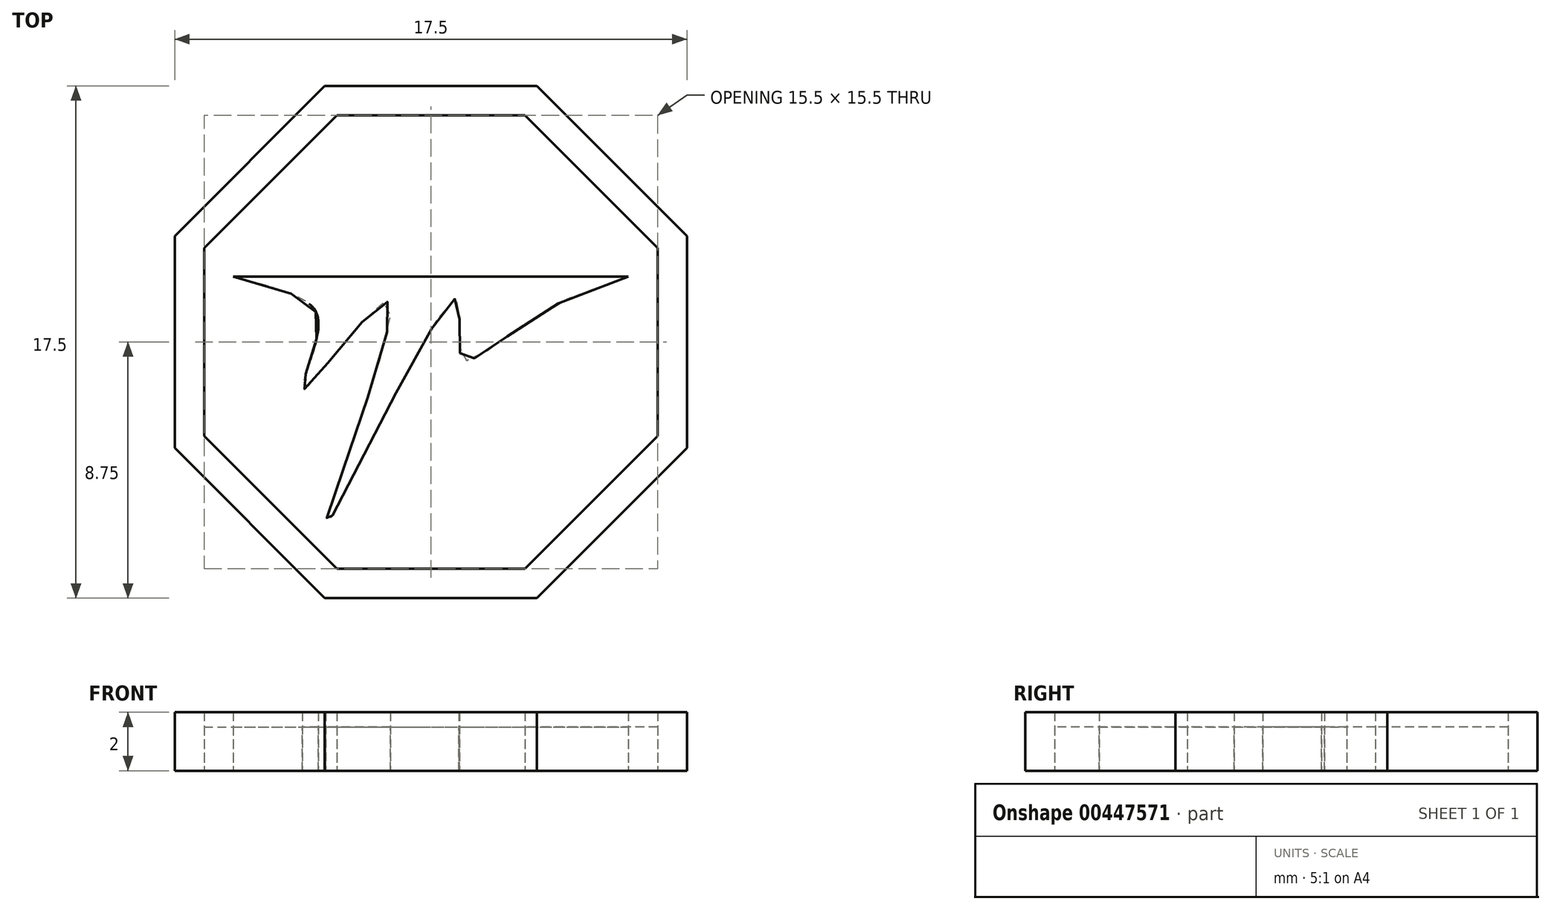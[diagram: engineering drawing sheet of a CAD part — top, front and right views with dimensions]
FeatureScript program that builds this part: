
annotation { "Feature Type Name" : "Feature", "Feature Type Description" : "" }
export const myFeature = defineFeature(function(context is Context, id is Id, definition is map)
    precondition{}
    {
        {
            var Q0;
            Q0=qCreatedBy(makeId("Top.planeOp"),FACE);
            var sketch = newSketch(context, id + "F0", { "sketchPlane" : qUnion([Q0])});
            skCircle(sketch, "E0.cCircle", {"center": v(0, 0) * mm, "radius": 8.75 * mm, "construction": true});
            skLineSegment(sketch, "E0.0", {"start": v(3.62, -8.75) * mm, "end": v(-3.62, -8.75) * mm});
            skLineSegment(sketch, "E0.1", {"start": v(-3.62, -8.75) * mm, "end": v(-8.75, -3.62) * mm});
            skLineSegment(sketch, "E0.2", {"start": v(-8.75, -3.62) * mm, "end": v(-8.75, 3.62) * mm});
            skLineSegment(sketch, "E0.3", {"start": v(-8.75, 3.62) * mm, "end": v(-3.62, 8.75) * mm});
            skLineSegment(sketch, "E0.4", {"start": v(-3.62, 8.75) * mm, "end": v(3.62, 8.75) * mm});
            skLineSegment(sketch, "E0.5", {"start": v(3.62, 8.75) * mm, "end": v(8.75, 3.62) * mm});
            skLineSegment(sketch, "E0.6", {"start": v(8.75, 3.62) * mm, "end": v(8.75, -3.62) * mm});
            skLineSegment(sketch, "E0.7", {"start": v(8.75, -3.62) * mm, "end": v(3.62, -8.75) * mm});
            skPoint(sketch, "E0.0.midPoint", {"position": v(0, -8.75) * mm});
            skCircle(sketch, "E1.cCircle", {"center": v(0, 0) * mm, "radius": 7.75 * mm, "construction": true});
            skLineSegment(sketch, "E1.0", {"start": v(7.75, -3.21) * mm, "end": v(3.21, -7.75) * mm});
            skLineSegment(sketch, "E1.1", {"start": v(3.21, -7.75) * mm, "end": v(-3.21, -7.75) * mm});
            skLineSegment(sketch, "E1.2", {"start": v(-3.21, -7.75) * mm, "end": v(-7.75, -3.21) * mm});
            skLineSegment(sketch, "E1.3", {"start": v(-7.75, -3.21) * mm, "end": v(-7.75, 3.21) * mm});
            skLineSegment(sketch, "E1.4", {"start": v(-7.75, 3.21) * mm, "end": v(-3.21, 7.75) * mm});
            skLineSegment(sketch, "E1.5", {"start": v(-3.21, 7.75) * mm, "end": v(3.21, 7.75) * mm});
            skLineSegment(sketch, "E1.6", {"start": v(3.21, 7.75) * mm, "end": v(7.75, 3.21) * mm});
            skLineSegment(sketch, "E1.7", {"start": v(7.75, 3.21) * mm, "end": v(7.75, -3.21) * mm});
            skPoint(sketch, "E1.0.midPoint", {"position": v(5.48, -5.48) * mm});
            skLineSegment(sketch, "E2", {"start": v(-6.75, 2.24) * mm, "end": v(6.75, 2.24) * mm});
            skFitSpline(sketch, "E3", {"points": [v(-6.75, 2.24) * mm, v(-3.88, 0.26) * mm, v(-4.32, -1.6) * mm, v(-1.44, 1.35) * mm, v(-3.59, -6.22) * mm, v(0.81, 1.47) * mm, v(1.02, -0.47) * mm, v(6.75, 2.24) * mm], "startDerivative": vector(61.17, -15.56) * mm, "endDerivative": vector(62.28, 14.38) * mm});
            skSolve(sketch);
        }
        {
            var Q0;
            Q0=makeQuery(id+"F0.imprint","IMPRINT",FACE,{"disambiguationData":[TD([[makeQuery(id+"F0.imprint","IMPRINT",EDGE,{"derivedFrom":sQuery(id+"F0.wireOp",EDGE,"E0.0")}),-1.0]])]});
            var Q1;
            Q1=makeQuery(id+"F0.imprint","IMPRINT",FACE,{"disambiguationData":[TD([[makeQuery(id+"F0.imprint","IMPRINT",EDGE,{"derivedFrom":sQuery(id+"F0.wireOp",EDGE,"E2")}),-1.0]])]});
            extrude(context, id + "F1", {"entities" : qUnion([Q0, Q1]), "depth" : 2 * mm});
        }
        {
            var Q0;
            Q0=makeQuery(id+"F0.imprint","IMPRINT",FACE,{"disambiguationData":[TD([[makeQuery(id+"F0.imprint","IMPRINT",EDGE,{"derivedFrom":sQuery(id+"F0.wireOp",EDGE,"E1.0")}),-1.0]])]});
            extrude(context, id + "F2", {"entities" : qUnion([Q0]), "depth" : 1.5 * mm});
        }
    });
